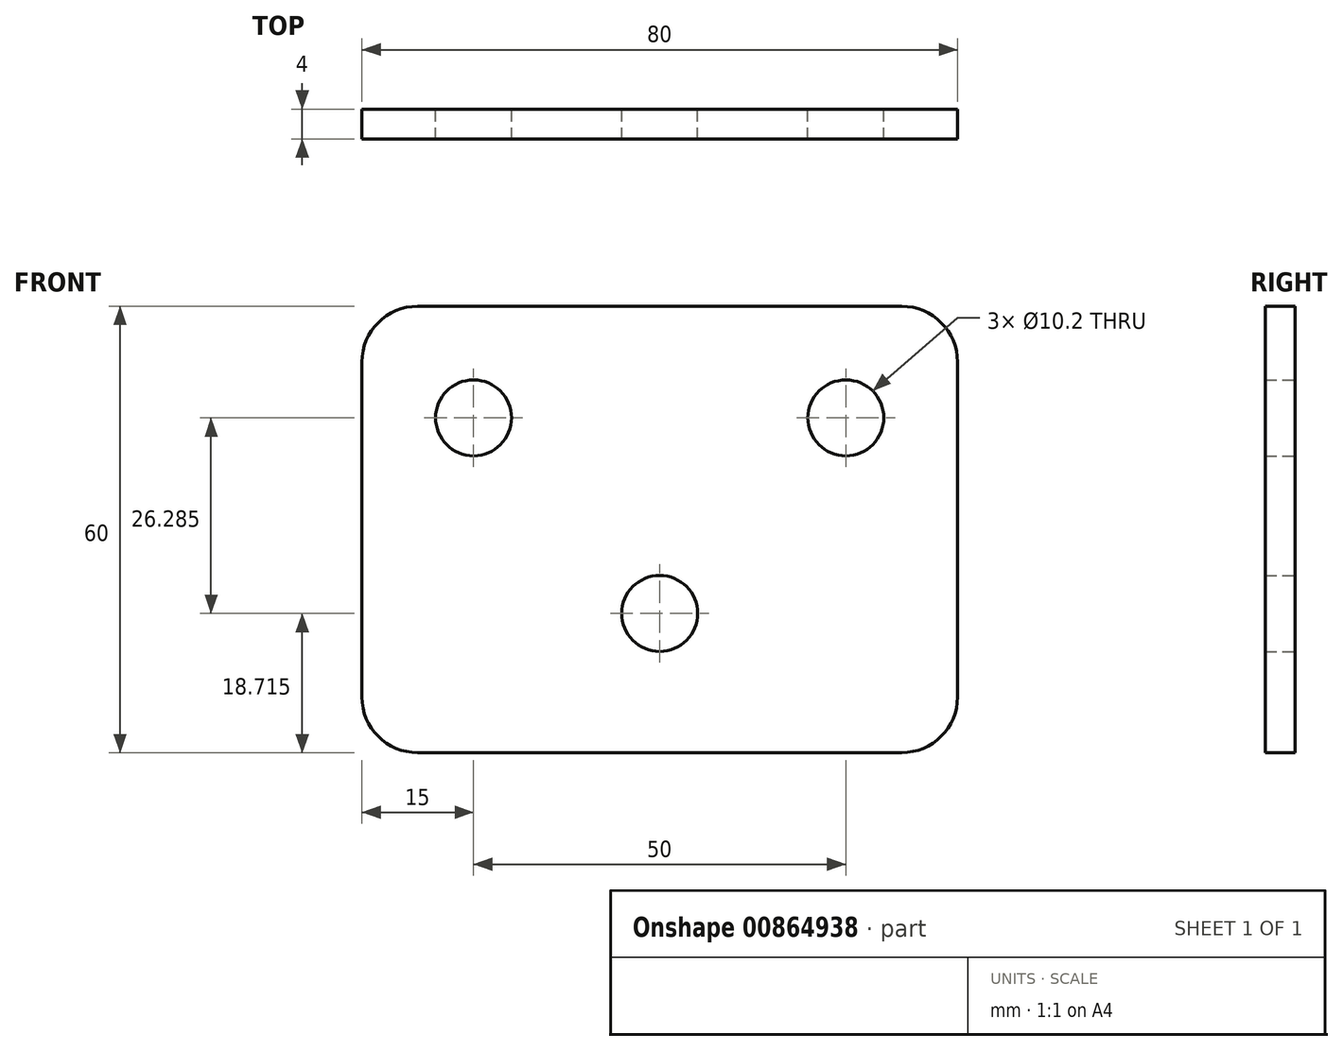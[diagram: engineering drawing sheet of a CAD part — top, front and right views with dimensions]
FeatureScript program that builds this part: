
annotation { "Feature Type Name" : "Feature", "Feature Type Description" : "" }
export const myFeature = defineFeature(function(context is Context, id is Id, definition is map)
    precondition{}
    {
        {
            var Q0;
            Q0=qCreatedBy(makeId("Front.planeOp"),FACE);
            var sketch = newSketch(context, id + "F0", { "sketchPlane" : qUnion([Q0])});
            skLineSegment(sketch, "E0.bottom", {"start": v(32.5, 30) * mm, "end": v(-32.5, 30) * mm});
            skLineSegment(sketch, "E0.top", {"start": v(32.5, -30) * mm, "end": v(-32.5, -30) * mm});
            skLineSegment(sketch, "E0.left", {"start": v(40, 22.5) * mm, "end": v(40, -22.5) * mm});
            skLineSegment(sketch, "E0.right", {"start": v(-40, 22.5) * mm, "end": v(-40, -22.5) * mm});
            skPoint(sketch, "E0.middle", {"position": v(0, 0) * mm});
            skCircle(sketch, "E1", {"center": v(-25, 15) * mm, "radius": 5.1 * mm});
            skCircle(sketch, "E2", {"center": v(25, 15) * mm, "radius": 5.1 * mm});
            skCircle(sketch, "E3", {"center": v(0, -11.29) * mm, "radius": 5.1 * mm});
            skPoint(sketch, "E4.visualSharp", {"position": v(-40, 30) * mm});
            skArc(sketch, "E4.filletArc", {"start": v(-32.5, 30) * mm, "mid": v(-37.8, 27.8) * mm, "end": v(-40, 22.5) * mm});
            skPoint(sketch, "E5.visualSharp", {"position": v(40, 30) * mm});
            skArc(sketch, "E5.filletArc", {"start": v(40, 22.5) * mm, "mid": v(37.8, 27.8) * mm, "end": v(32.5, 30) * mm});
            skPoint(sketch, "E6.visualSharp", {"position": v(40, -30) * mm});
            skArc(sketch, "E6.filletArc", {"start": v(32.5, -30) * mm, "mid": v(37.8, -27.8) * mm, "end": v(40, -22.5) * mm});
            skPoint(sketch, "E7.visualSharp", {"position": v(-40, -30) * mm});
            skArc(sketch, "E7.filletArc", {"start": v(-40, -22.5) * mm, "mid": v(-37.8, -27.8) * mm, "end": v(-32.5, -30) * mm});
            skSolve(sketch);
        }
        {
            var Q0;
            Q0 = qSketchRegion(id + "F0", true);
            extrude(context, id + "F1", {"entities" : qUnion([Q0]), "depth" : 4 * mm, "offsetDistance" : 25 * mm});
        }
    });
